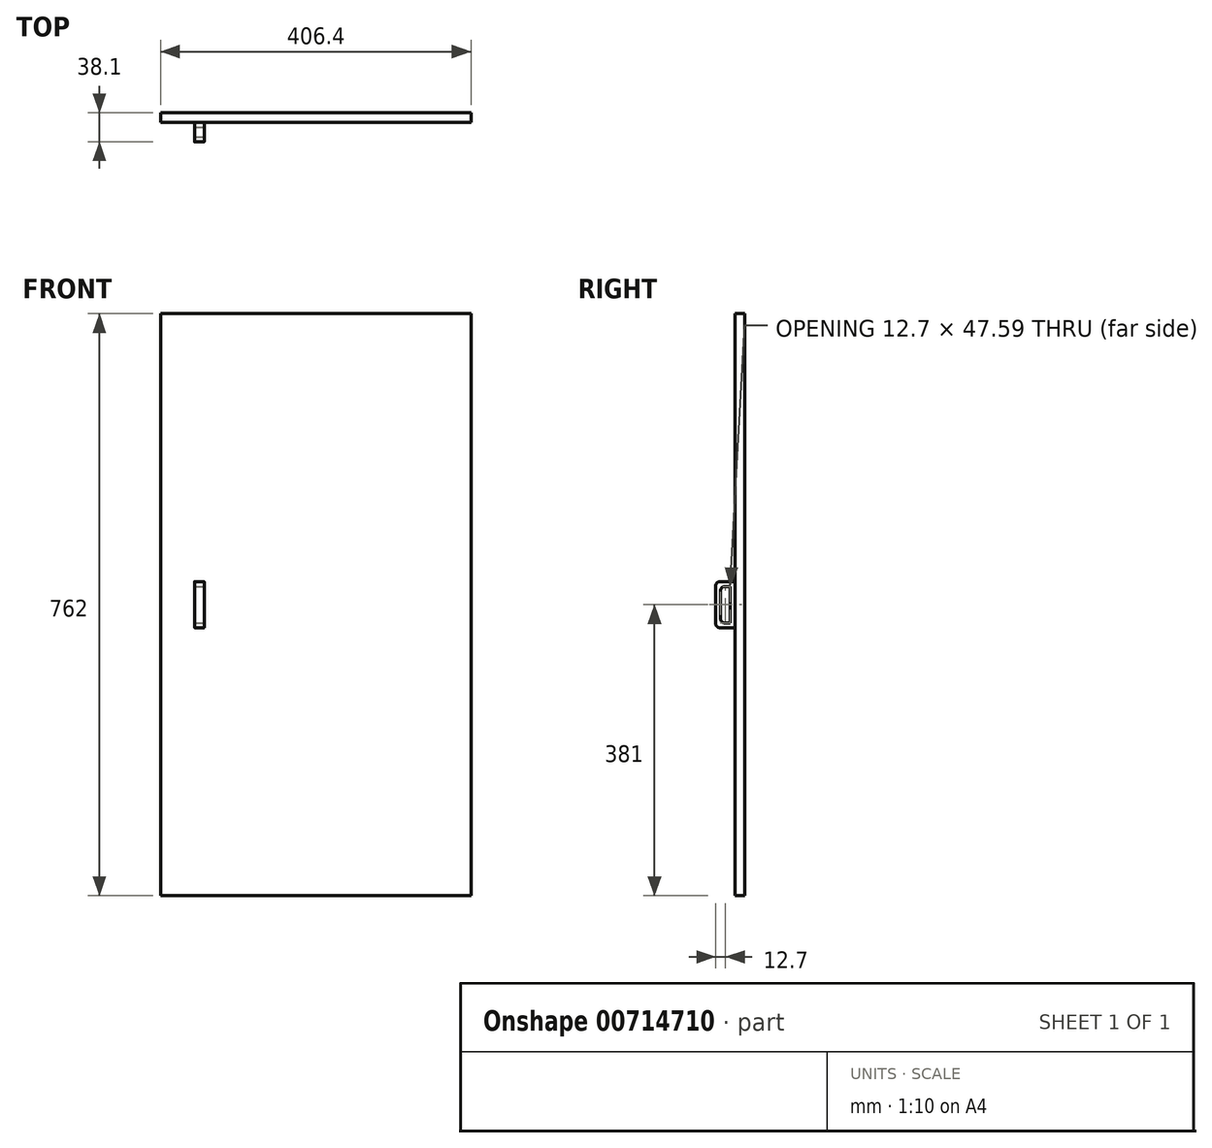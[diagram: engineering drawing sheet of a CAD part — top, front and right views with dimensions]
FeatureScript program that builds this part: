
annotation { "Feature Type Name" : "Feature", "Feature Type Description" : "" }
export const myFeature = defineFeature(function(context is Context, id is Id, definition is map)
    precondition{}
    {
        {
            var Q0;
            Q0=qCreatedBy(makeId("Front.planeOp"),FACE);
            var sketch = newSketch(context, id + "F0", { "sketchPlane" : qUnion([Q0])});
            skLineSegment(sketch, "E0.bottom", {"start": v(203.2, 381) * mm, "end": v(-203.2, 381) * mm});
            skLineSegment(sketch, "E0.top", {"start": v(203.2, -381) * mm, "end": v(-203.2, -381) * mm});
            skLineSegment(sketch, "E0.left", {"start": v(203.2, 381) * mm, "end": v(203.2, -381) * mm});
            skLineSegment(sketch, "E0.right", {"start": v(-203.2, 381) * mm, "end": v(-203.2, -381) * mm});
            skPoint(sketch, "E0.middle", {"position": v(0, 0) * mm});
            skSolve(sketch);
        }
        {
            var Q0;
            Q0 = qSketchRegion(id + "F0", true);
            extrude(context, id + "F1", {"entities" : qUnion([Q0]), "depth" : 12.7 * mm, "offsetDistance" : 25.4 * mm});
        }
        {
            var Q0;
            Q0=makeQuery(id+"F1.opExtrude","CAP_FACE",FACE,{"disambiguationData":[OSD([sQuery(id+"F0.wireOp",EDGE,"E0.bottom"),sQuery(id+"F0.wireOp",EDGE,"E0.top"),sQuery(id+"F0.wireOp",EDGE,"E0.left"),sQuery(id+"F0.wireOp",EDGE,"E0.right")])],"isStart":false});
            var sketch = newSketch(context, id + "F2", { "sketchPlane" : qUnion([Q0])});
            skLineSegment(sketch, "E1", {"start": v(-203.2, 0) * mm, "end": v(-152.4, 0) * mm});
            skLineSegment(sketch, "E2.bottom", {"start": v(-146.05, 30.15) * mm, "end": v(-158.75, 30.15) * mm});
            skLineSegment(sketch, "E2.top", {"start": v(-146.05, -30.15) * mm, "end": v(-158.75, -30.15) * mm});
            skLineSegment(sketch, "E2.left", {"start": v(-146.05, 30.15) * mm, "end": v(-146.05, -30.15) * mm});
            skLineSegment(sketch, "E2.right", {"start": v(-158.75, 30.15) * mm, "end": v(-158.75, -30.15) * mm});
            skPoint(sketch, "E2.middle", {"position": v(-152.4, 0) * mm});
            skSolve(sketch);
        }
        {
            var Q0;
            Q0 = qSketchRegion(id + "F2", true);
            extrude(context, id + "F3", {"entities" : qUnion([Q0]), "operationType" : NewBodyOperationType.ADD, "depth" : 25.4 * mm, "offsetDistance" : 25.4 * mm});
        }
        {
            var Q0;
            Q0=makeQuery(id+"F3.opExtrude","SWEPT_FACE",FACE,{"disambiguationData":[OSD([sQuery(id+"F2.wireOp",EDGE,"E2.left")])]});
            var sketch = newSketch(context, id + "F4", { "sketchPlane" : qUnion([Q0])});
            skLineSegment(sketch, "E3", {"start": v(-38.1, 0) * mm, "end": v(-25.4, 0) * mm});
            skLineSegment(sketch, "E4.bottom", {"start": v(-19.05, 23.8) * mm, "end": v(-31.75, 23.8) * mm});
            skLineSegment(sketch, "E4.top", {"start": v(-19.05, -23.8) * mm, "end": v(-31.75, -23.8) * mm});
            skLineSegment(sketch, "E4.left", {"start": v(-19.05, 23.8) * mm, "end": v(-19.05, -23.8) * mm});
            skLineSegment(sketch, "E4.right", {"start": v(-31.75, 23.8) * mm, "end": v(-31.75, -23.8) * mm});
            skPoint(sketch, "E4.middle", {"position": v(-25.4, 0) * mm});
            skSolve(sketch);
        }
        {
            var Q0;
            {var subQ1=sQuery(id+"F4.wireOp",EDGE,"E4.bottom");Q0=makeQuery(id+"F4.imprint","IMPRINT",FACE,{"disambiguationData":[TD([[makeQuery(id+"F4.imprint","IMPRINT",EDGE,{"derivedFrom":subQ1}),1.0]])]});}
            extrude(context, id + "F5", {"entities" : qUnion([Q0]), "operationType" : NewBodyOperationType.REMOVE, "oppositeDirection" : true, "depth" : 86.36 * mm, "offsetDistance" : 25.4 * mm});
        }
        {
            var Q0;
            Q0=makeQuery(id+"F3.opExtrude","CAP_EDGE",EDGE,{"disambiguationData":[OSD([sQuery(id+"F2.wireOp",EDGE,"E2.bottom")])],"isStart":false});
            var Q1;
            Q1=makeQuery(id+"F3.opExtrude","CAP_EDGE",EDGE,{"disambiguationData":[OSD([sQuery(id+"F2.wireOp",EDGE,"E2.top")])],"isStart":false});
            var Q2;
            Q2=makeQuery(id+"F5.boolean.opBoolean","COPY",EDGE,{"derivedFrom":makeQuery(id+"F5.opExtrude","SWEPT_EDGE",EDGE,{"disambiguationData":[OSD([sQuery(id+"F4.wireOp",EDGE,"E4.bottom"),sQuery(id+"F4.wireOp",EDGE,"E4.right")])]})});
            var Q3;
            Q3=makeQuery(id+"F5.boolean.opBoolean","COPY",EDGE,{"derivedFrom":makeQuery(id+"F5.opExtrude","SWEPT_EDGE",EDGE,{"disambiguationData":[OSD([sQuery(id+"F4.wireOp",EDGE,"E4.top"),sQuery(id+"F4.wireOp",EDGE,"E4.right")])]})});
            fillet(context, id + "F6", {"entities" : qUnion([Q0, Q1, Q2, Q3]), "radius" : 5.08 * mm, "tangentPropagation" : true, "allowEdgeOverflow" : false});
        }
    });
